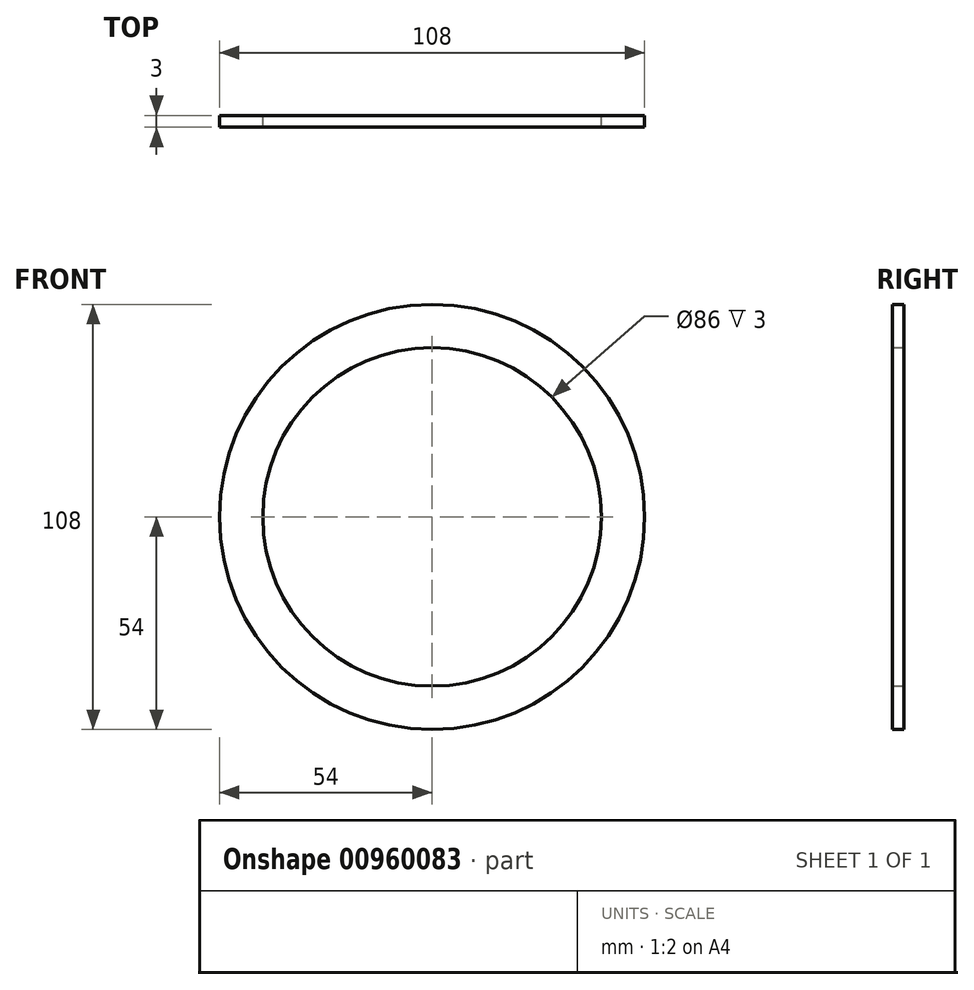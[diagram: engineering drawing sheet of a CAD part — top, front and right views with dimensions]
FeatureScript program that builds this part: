
annotation { "Feature Type Name" : "Feature", "Feature Type Description" : "" }
export const myFeature = defineFeature(function(context is Context, id is Id, definition is map)
    precondition{}
    {
        {
            var Q0;
            Q0=qCreatedBy(makeId("Front.planeOp"),FACE);
            var sketch = newSketch(context, id + "F0", { "sketchPlane" : qUnion([Q0])});
            skCircle(sketch, "E0", {"center": v(0, 0) * mm, "radius": 43 * mm});
            skCircle(sketch, "E1", {"center": v(0, 0) * mm, "radius": 54 * mm});
            skSolve(sketch);
        }
        {
            var Q0;
            Q0=makeQuery(id+"F0.imprint","IMPRINT",FACE,{"disambiguationData":[TD([[makeQuery(id+"F0.imprint","IMPRINT",EDGE,{"derivedFrom":sQuery(id+"F0.wireOp",EDGE,"E0")}),-1.0]])]});
            extrude(context, id + "F1", {"entities" : qUnion([Q0]), "depth" : 3 * mm, "offsetDistance" : 25 * mm});
        }
    });
